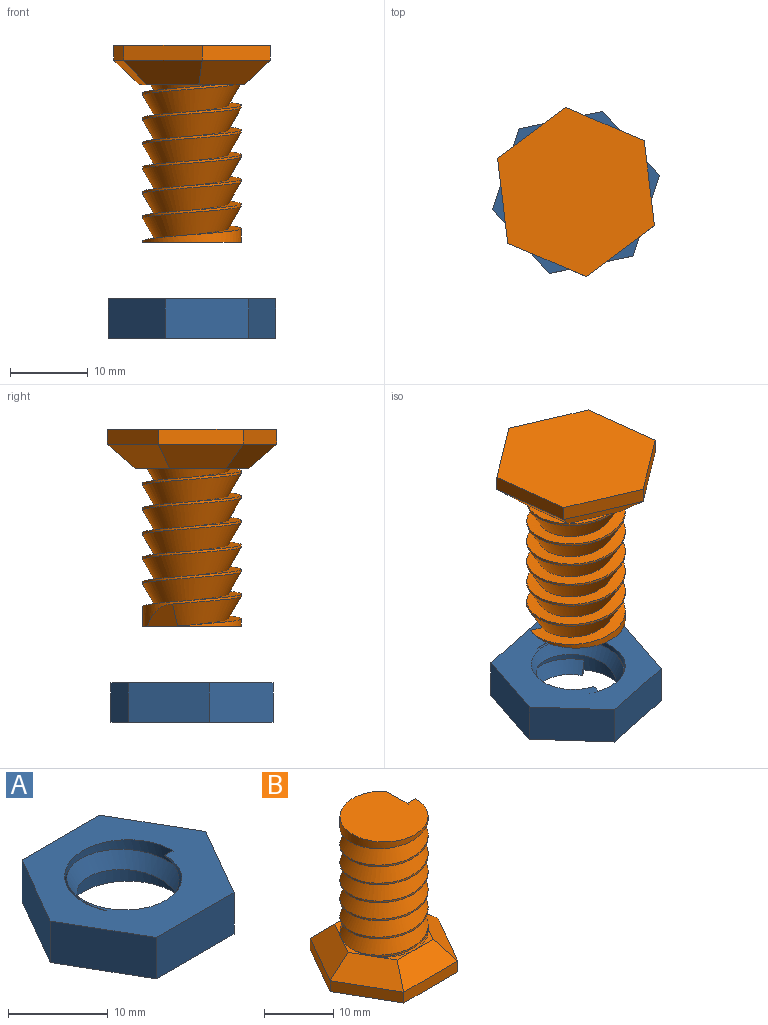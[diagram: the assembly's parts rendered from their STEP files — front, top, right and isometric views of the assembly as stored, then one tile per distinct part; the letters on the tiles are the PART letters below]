
ASSEMBLY  parts=2 mates=1
PART A: 15 faces, bbox 22.1x19.2x7.2 mm
  f0: plane 22.1x19.15mm, normal (0,0,1), area 201.3mm2, adj f1,f2,f3,f4,f5,f6,f7,f9
  f1: plane 9.53x5.5mm, normal (0.87,-0.5,0), area 55.9mm2, adj f0,f2,f7,f8
  f2: plane 9.53x5.5mm, normal (0.87,0.5,0), area 55.9mm2, adj f0,f1,f3,f8
  f3: plane 11x5.08mm, normal (0,1,0), area 55.9mm2, adj f0,f2,f4,f8
  f4: plane 9.53x5.5mm, normal (-0.87,0.5,0), area 55.9mm2, adj f0,f3,f5,f8
  f5: plane 9.53x5.5mm, normal (-0.87,-0.5,0), area 55.9mm2, adj f0,f4,f7,f8
  f6: cylinder r=6.35mm len=12.7mm, axis (0,0,-1), area 124.5mm2, adj f0,f8,f9,f11,f12,f14
  f7: plane 11x5.08mm, normal (0,-1,0), area 55.9mm2, adj f0,f1,f5,f8
  f8: plane 22x19.05mm, normal (0,0,-1), area 187.1mm2, adj f1,f2,f3,f4,f5,f6,f7,f10
  f9: bspline ~16.54x14.33mm, area 17.8mm2, adj f0,f6,f12,f13
  f10: bspline ~6.2x4.09mm, area 0mm2, adj f8,f12,f14
  f11: plane 1.22x0.04mm, normal (0,1,0), area 0.1mm2, adj f0,f6,f13,f14
  f12: plane 1.76x1.65mm, normal (0.59,0.81,0), area 1.3mm2, adj f6,f8,f9,f10,f13,f14
  f13: bspline ~14.2x12.29mm, area 95.7mm2, adj f0,f9,f11,f12,f14
  f14: bspline ~16.54x14.33mm, area 71.1mm2, adj f6,f8,f10,f11,f12,f13
PART B: 26 faces, bbox 22x19.1x25.4 mm
  f0: plane 5.51x3.18mm, normal (0,0,1), area 2.2mm2, adj f16,f19,f21
  f1: plane 6.37x1.85mm, normal (0,0,1), area 2.2mm2, adj f5,f16,f18,f21,f23
  f2: plane 5.5x3.18mm, normal (0,0,1), area 2.2mm2, adj f5,f16,f23,f24
  f3: plane 5.51x3.18mm, normal (0,0,1), area 2.2mm2, adj f16,f22,f24
  f4: plane 6.37x1.85mm, normal (0,0,1), area 2.2mm2, adj f16,f20,f22
  f5: cylinder r=6.35mm len=20.32mm, axis (0,0,-1), area 259.7mm2, adj f1,f2,f6,f17,f18,f25
  f6: plane 12.7x12.7mm, normal (0,0,1), area 121.7mm2, adj f5,f17,f18,f25
  f7: plane 9.53x5.5mm, normal (0.87,-0.5,0), area 21mm2, adj f8,f12,f14,f22
  f8: plane 9.53x5.5mm, normal (0.87,0.5,0), area 21mm2, adj f7,f9,f14,f20
  f9: plane 11x1.91mm, normal (0,1,0), area 21mm2, adj f8,f10,f14,f19
  f10: plane 9.53x5.5mm, normal (-0.87,0.5,0), area 21mm2, adj f9,f11,f14,f21
  f11: plane 9.53x5.5mm, normal (-0.87,-0.5,0), area 21mm2, adj f10,f12,f14,f23
  f12: plane 11x1.91mm, normal (0,-1,0), area 21mm2, adj f7,f11,f14,f24
  f13: plane 5.51x3.18mm, normal (0,0,1), area 2.2mm2, adj f16,f19,f20
  f14: plane 22x19.05mm, normal (0,0,-1), area 314.3mm2, adj f7,f8,f9,f10,f11,f12
  f15: plane 2.89x1.35mm, normal (0.59,-0.81,0), area 2.4mm2, adj f16,f17,f18
  f16: cylinder r=6.35mm len=12.7mm, axis (0,0,-1), area 52.3mm2, adj f0,f1,f2,f3,f4,f13,f15,f18
  f17: bspline ~20.64x14.67mm, area 370.9mm2, adj f5,f6,f15,f18
  f18: bspline ~23.52x14.67mm, area 777.8mm2, adj f1,f5,f6,f15,f16,f17,f25
  f19: plane 11x3.18mm, normal (0,0.71,0.71), area 41.2mm2, adj f0,f9,f13,f20,f21
  f20: plane 9.53x7.33mm, normal (0.61,0.35,0.71), area 41.2mm2, adj f4,f8,f13,f19,f22
  f21: plane 9.53x7.33mm, normal (-0.61,0.35,0.71), area 41.2mm2, adj f0,f1,f10,f19,f23
  f22: plane 9.53x7.33mm, normal (0.61,-0.35,0.71), area 41.2mm2, adj f3,f4,f7,f20,f24
  f23: plane 9.53x7.33mm, normal (-0.61,-0.35,0.71), area 41.2mm2, adj f1,f2,f11,f21,f24
  f24: plane 11x3.18mm, normal (0,-0.71,0.71), area 41.2mm2, adj f2,f3,f12,f22,f23
  f25: plane 4.29x2.88mm, normal (0.87,0,0.5), area 9.8mm2, adj f5,f6,f18
PLACE A rot(axis=(0,0,-1),108.3deg) t=(39.07,9.92,0)mm fixed
PLACE B rot(axis=(-0.2,-0.98,0),180deg) t=(15.03,-1.51,37.76)mm
MATE cylindrical A.f6 <-> B.f5  axis (0,0,-1) through (32.78,-9.08,0)mm
